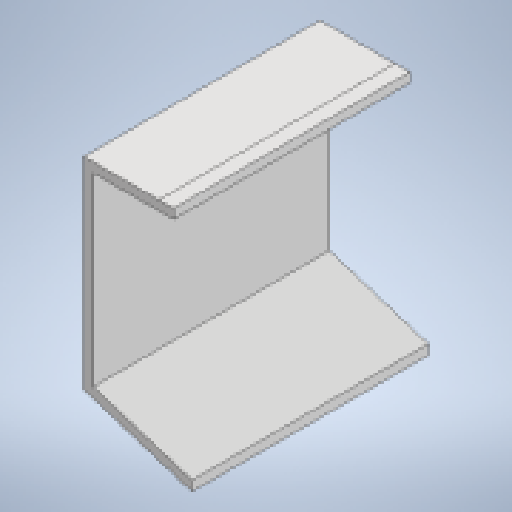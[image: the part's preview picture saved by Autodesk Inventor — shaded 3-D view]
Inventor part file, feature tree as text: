
AUTODESK INVENTOR PART (.ipt)
format: ipt  version: 2023 (Build 270158000, 158)  size: 137,728 bytes
history: native  units: in
note: dims shown in document units (in); Inventor stores cm internally (conversion verified against a paired STEP export)
features: reference x6, other x5, extrude x1, sketch x1
ambient origin geometry x8: Origin, YZ Plane, XZ Plane, XY Plane, X Axis, Y Axis, Z Axis, Center Point
bodies: Body1 (feature_tree)
feature tree (13):
  other  "Bryła1"
  extrude  "Wyciągnięcie proste1"  Depth=0.0787in
  sketch  "Szkic1"
  reference  "Odniesienie1"
  reference  "Odniesienie2"
  reference  "Odniesienie3"
  reference  "Odniesienie4"
  reference  "Odniesienie5"
  reference  "Odniesienie6"
  other  "Zespół2"
  other  "spod:1"
  other  "kolko:1"
  other  "TOF_VL53L0X (1):3"
